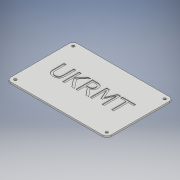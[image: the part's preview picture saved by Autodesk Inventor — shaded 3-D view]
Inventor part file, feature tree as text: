
AUTODESK INVENTOR PART (.ipt)
format: ipt  version: 2018.3 (Build 223284000, 284)  size: 210,432 bytes
history: native  units: mm
features: sketch x2, extrude x1, chamfer x1, emboss x1
ambient origin geometry x8: Origin, YZ Plane, XZ Plane, XY Plane, X Axis, Y Axis, Z Axis, Center Point
bodies: Solid1 (feature_tree)
feature tree (5):
  extrude  "Extrusion1"  Depth=101.6mm
  chamfer  "Chamfer1"  Distance=4.0mm
  emboss  "Emboss1"
  sketch  "Sketch1"  dims[d0=152.4mm d1=101.6mm]
  sketch  "Sketch2"  dims[d2=7.0mm d3=4.0mm d4=4.0mm d5=4.0mm d6=4.0mm d7=2.0mm d8=0.0mm d9=0.5mm d10=2.0mm d11=45.0deg d12=1.0mm d13=0.0mm]
